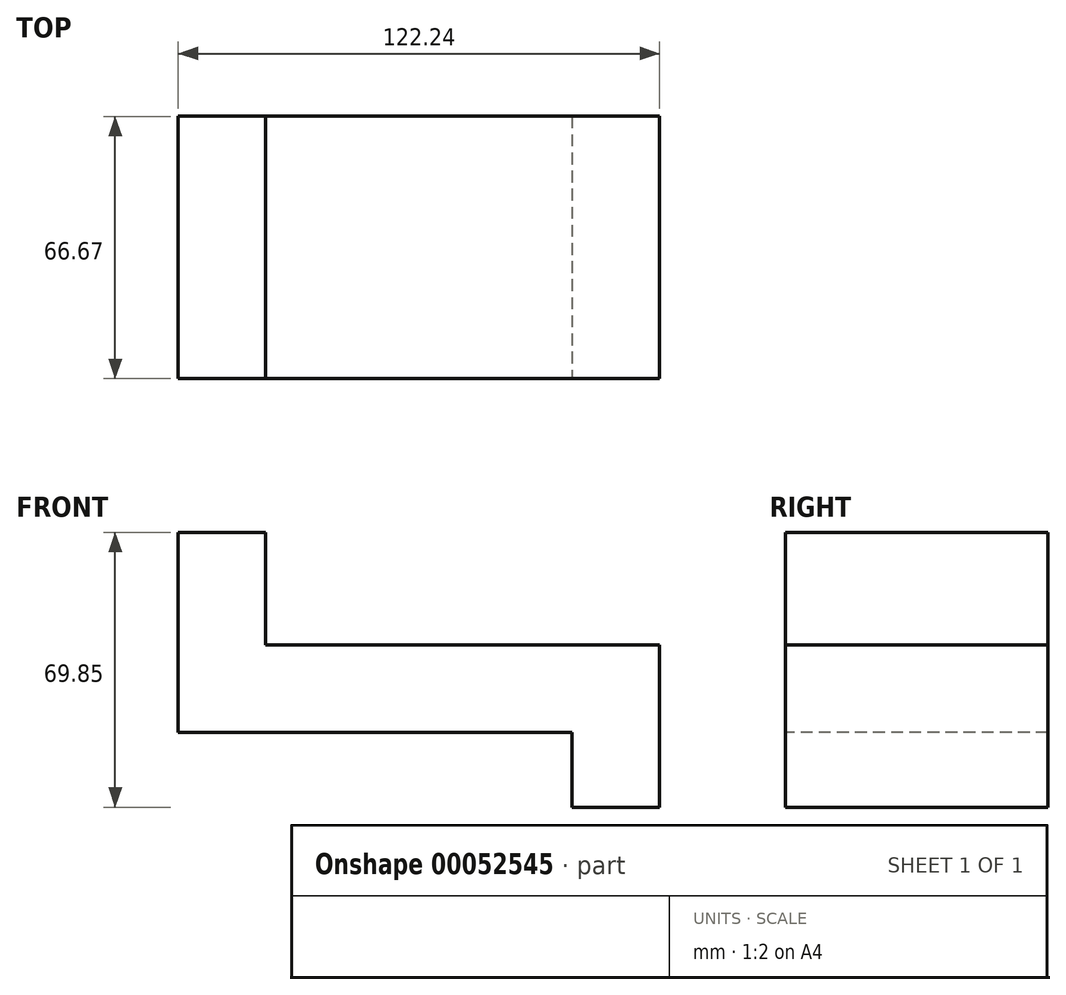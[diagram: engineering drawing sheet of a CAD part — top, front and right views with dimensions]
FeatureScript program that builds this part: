
annotation { "Feature Type Name" : "Feature", "Feature Type Description" : "" }
export const myFeature = defineFeature(function(context is Context, id is Id, definition is map)
    precondition{}
    {
        {
            var Q0;
            Q0=qCreatedBy(makeId("Front.planeOp"),FACE);
            var sketch = newSketch(context, id + "F0", { "sketchPlane" : qUnion([Q0])});
            skLineSegment(sketch, "E0", {"start": v(-86.8, -5.65) * mm, "end": v(13.21, -5.65) * mm});
            skLineSegment(sketch, "E1", {"start": v(13.21, -5.65) * mm, "end": v(13.21, -24.7) * mm});
            skLineSegment(sketch, "E2", {"start": v(13.21, -24.7) * mm, "end": v(35.44, -24.7) * mm});
            skLineSegment(sketch, "E3", {"start": v(35.44, -24.7) * mm, "end": v(35.44, 16.57) * mm});
            skLineSegment(sketch, "E4", {"start": v(35.44, 16.57) * mm, "end": v(-64.57, 16.57) * mm});
            skLineSegment(sketch, "E5", {"start": v(-64.57, 16.57) * mm, "end": v(-64.57, 45.15) * mm});
            skLineSegment(sketch, "E6", {"start": v(-64.57, 45.15) * mm, "end": v(-86.8, 45.15) * mm});
            skLineSegment(sketch, "E7", {"start": v(-86.8, 45.15) * mm, "end": v(-86.8, -5.65) * mm});
            skPoint(sketch, "E8.orphan", {"position": v(35.44, -5.65) * mm});
            skPoint(sketch, "E9.orphan", {"position": v(-73.94, -5.65) * mm});
            skSolve(sketch);
        }
        {
            var Q0;
            Q0 = qSketchRegion(id + "F0", true);
            extrude(context, id + "F1", {"entities" : qUnion([Q0]), "oppositeDirection" : true, "depth" : 66.67 * mm});
        }
    });
